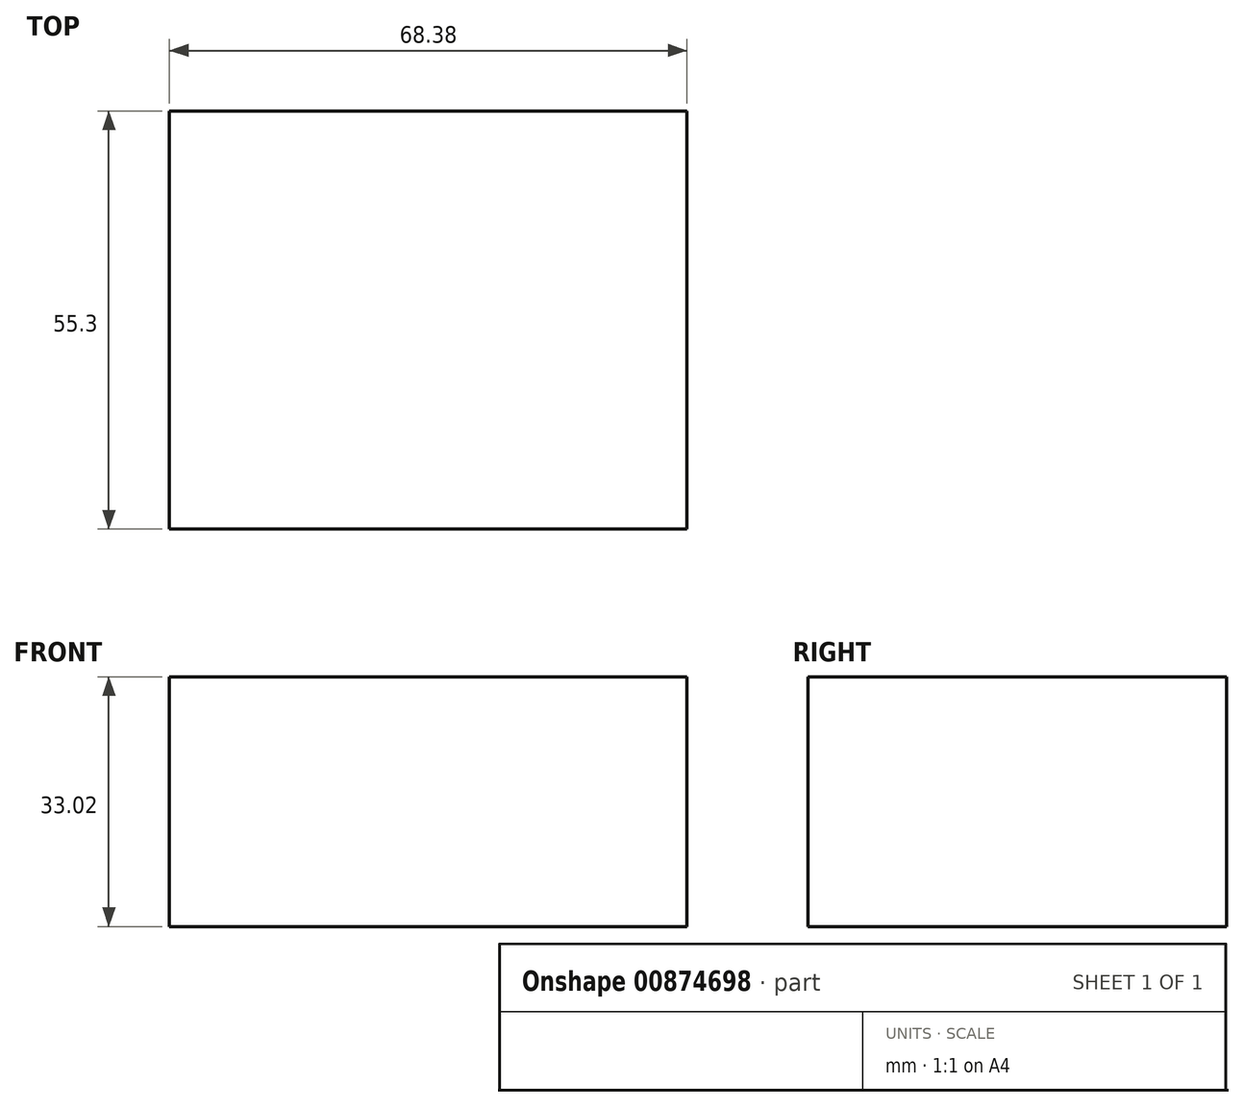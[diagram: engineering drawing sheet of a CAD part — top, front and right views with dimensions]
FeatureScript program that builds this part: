
annotation { "Feature Type Name" : "Feature", "Feature Type Description" : "" }
export const myFeature = defineFeature(function(context is Context, id is Id, definition is map)
    precondition{}
    {
        {
            var Q0;
            Q0=qCreatedBy(makeId("Top.planeOp"),FACE);
            var sketch = newSketch(context, id + "F0", { "sketchPlane" : qUnion([Q0])});
            skLineSegment(sketch, "E0.bottom", {"start": v(34.19, -27.65) * mm, "end": v(-34.19, -27.65) * mm});
            skLineSegment(sketch, "E0.top", {"start": v(34.19, 27.65) * mm, "end": v(-34.19, 27.65) * mm});
            skLineSegment(sketch, "E0.left", {"start": v(34.19, -27.65) * mm, "end": v(34.19, 27.65) * mm});
            skLineSegment(sketch, "E0.right", {"start": v(-34.19, -27.65) * mm, "end": v(-34.19, 27.65) * mm});
            skPoint(sketch, "E0.middle", {"position": v(0, 0) * mm});
            skSolve(sketch);
        }
        {
            var Q0;
            Q0=makeQuery(id+"F0.imprint","IMPRINT",FACE,{"disambiguationData":[TD([[makeQuery(id+"F0.imprint","IMPRINT",EDGE,{"derivedFrom":sQuery(id+"F0.wireOp",EDGE,"E0.bottom")}),-1.0]])]});
            extrude(context, id + "F1", {"entities" : qUnion([Q0]), "depth" : 33.02 * mm, "offsetDistance" : 25.4 * mm});
        }
    });
